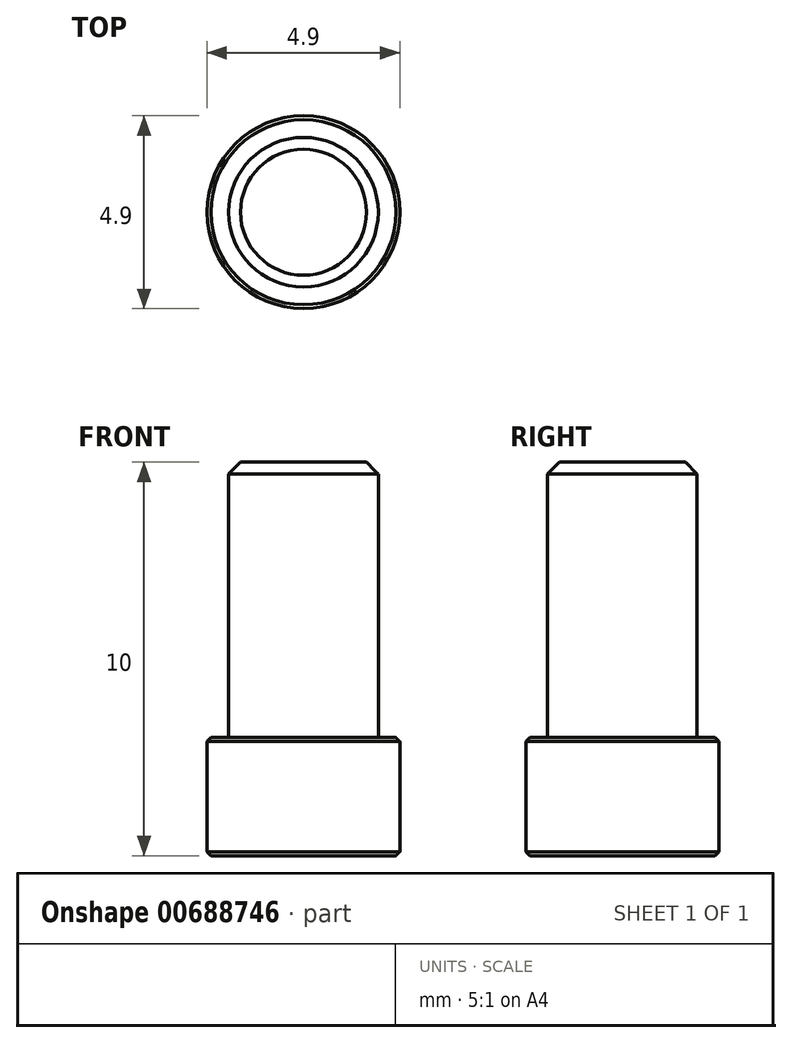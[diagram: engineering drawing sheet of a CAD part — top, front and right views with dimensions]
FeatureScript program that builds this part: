
annotation { "Feature Type Name" : "Feature", "Feature Type Description" : "" }
export const myFeature = defineFeature(function(context is Context, id is Id, definition is map)
    precondition{}
    {
        {
            var Q0;
            Q0=qCreatedBy(makeId("Top.planeOp"),FACE);
            var sketch = newSketch(context, id + "F0", { "sketchPlane" : qUnion([Q0])});
            skCircle(sketch, "E0", {"center": v(0, 0) * mm, "radius": 2.45 * mm});
            skCircle(sketch, "E1", {"center": v(0, 0) * mm, "radius": 1.9 * mm});
            skSolve(sketch);
        }
        {
            var Q0;
            Q0=makeQuery(id+"F0.imprint","IMPRINT",FACE,{"disambiguationData":[TD([[makeQuery(id+"F0.imprint","IMPRINT",EDGE,{"derivedFrom":sQuery(id+"F0.wireOp",EDGE,"E1")}),1.0]])]});
            extrude(context, id + "F1", {"entities" : qUnion([Q0]), "depth" : 10 * mm, "offsetDistance" : 25 * mm});
        }
        {
            var Q0;
            Q0=makeQuery(id+"F0.imprint","IMPRINT",FACE,{"disambiguationData":[TD([[makeQuery(id+"F0.imprint","IMPRINT",EDGE,{"derivedFrom":sQuery(id+"F0.wireOp",EDGE,"E0")}),1.0]])]});
            extrude(context, id + "F2", {"entities" : qUnion([Q0]), "operationType" : NewBodyOperationType.ADD, "depth" : 3 * mm, "offsetDistance" : 25 * mm});
        }
        {
            var Q0;
            Q0=makeQuery(id+"F1.opExtrude","CAP_EDGE",EDGE,{"disambiguationData":[OSD([sQuery(id+"F0.wireOp",EDGE,"E1")])],"isStart":false});
            chamfer(context, id + "F3", {"entities" : qUnion([Q0]), "width" : 0.3 * mm, "tangentPropagation" : true});
        }
        {
            var Q0;
            Q0=makeQuery(id+"F2.opExtrude","CAP_EDGE",EDGE,{"disambiguationData":[OSD([sQuery(id+"F0.wireOp",EDGE,"E0")])],"isStart":true});
            var Q1;
            Q1=makeQuery(id+"F2.opExtrude","CAP_EDGE",EDGE,{"disambiguationData":[OSD([sQuery(id+"F0.wireOp",EDGE,"E0")])],"isStart":false});
            chamfer(context, id + "F4", {"entities" : qUnion([Q0, Q1]), "width" : 0.1 * mm, "tangentPropagation" : true});
        }
    });
